# Revit family: APB_SUPPLY
name_source: partatom
category: Mechanical Equipment
units: mm (PartAtom-declared; Revit-internal decimal feet)

## family parameters
Always vertical = Yes
Cut with Voids When Loaded = No
Part Type = Normal
Room Calculation Point = No
Round Connector Dimension = Use Diameter
Shared = No
Work Plane-Based = No

## types (5) — shared parameters
0 = 0' - 0"
1" = 0' - 1"
1.5 = 0' - 1 1/2"
135 = 135.00°
2" = 0' - 2"
2' = 2' - 0"
3" = 0' - 3"
4" = 0' - 4"
9" = 0' - 9"
90 = 90.00°
HALF = 0' - 0 1/2"
Manufacturer = Loren Cook Company
Model = APB-Supply
ONE EIGTH = 0' - 0 1/8"
Type Comments = Axia-Pac Wall Supply Ventilator Cast Aluminum Propeller Belt Drive
URL = www.lorencook.com

## per-type parameters (varying)
- 24_APB_SUPPLY: (A/2)-1"=1' - 2 27/32"; (A/2)-C-.5"=0' - 7 27/32"; (D_SUP/2)-(C/2)-.125"=0' - 11 1/2"; (SIZE/2)-.25"=0' - 11 3/4"; -((A/2)-C-.5")=-0' - 7 27/32"; -((SIZE/2)-.25")=-0' - 11 3/4"; -B=-1' - 7 1/16"; -B+1"=-1' - 5 1/16"; -C/2=-0' - 3 3/8"; -D=-0' - 2"; -D_PAC/2=-1' - 9 3/16"; -WH_B/2=-1' - 5"; A=2' - 6 3/16"; A/2=1' - 3 3/32"; A/3.5=0' - 8 5/8"; A/7=0' - 4 5/16"; A_PAC=2' - 9 1/2"; A_PAC/2=1' - 4 3/4"; B=1' - 7 1/16"; B/2=0' - 9 17/32"; B/4=0' - 4 25/32"; B_PAC=2' - 7"; B_PAC/2=1' - 3 1/2"; C=0' - 6 3/4"; C/2=0' - 3 3/8"; C_PAC=2' - 3 1/2"; C_PAC/2=1' - 1 3/4"; D=0' - 2"; D/2=0' - 1"; D_PAC=2' - 10 3/8"; D_PAC/2=1' - 1 3/16"; D_SUP=2' - 6"; D_SUP/2=1' - 3"; MOTOR=0' - 3"; SIZE=2' - 0"; SIZE/2=1' - 0"; WH_A=2' - 3 1/8"; WH_B=2' - 10"; WH_B/2=1' - 5"; WH_C=3' - 1"; WO_PAC=2' - 7 1/4"; WO_PAC/2=1' - 3 5/8"
- 30_APB_SUPPLY: (A/2)-1"=1' - 5 27/32"; (A/2)-C-.5"=0' - 10 27/32"; (D_SUP/2)-(C/2)-.125"=1' - 2 1/2"; (SIZE/2)-.25"=1' - 2 3/4"; -((A/2)-C-.5")=-0' - 10 27/32"; -((SIZE/2)-.25")=-1' - 2 3/4"; -B=-1' - 7 1/16"; -B+1"=-1' - 5 1/16"; -C/2=-0' - 3 3/8"; -D=-0' - 3"; -D_PAC/2=-1' - 11"; -WH_B/2=-1' - 8"; A=3' - 0 3/16"; A/2=1' - 6 3/32"; A/3.5=0' - 10 11/32"; A/7=0' - 5 5/32"; A_PAC=3' - 3 1/2"; A_PAC/2=1' - 7 3/4"; B=1' - 7 1/16"; B/2=0' - 9 17/32"; B/4=0' - 4 25/32"; B_PAC=3' - 1"; B_PAC/2=1' - 6 1/2"; C=0' - 6 3/4"; C/2=0' - 3 3/8"; C_PAC=2' - 9 1/2"; C_PAC/2=1' - 4 3/4"; D=0' - 3"; D/2=0' - 1 1/2"; D_PAC=3' - 2"; D_PAC/2=1' - 3"; D_SUP=3' - 0"; D_SUP/2=1' - 6"; MOTOR=0' - 3 19/32"; SIZE=2' - 6"; SIZE/2=1' - 3"; WH_A=2' - 7 7/16"; WH_B=3' - 4"; WH_B/2=1' - 8"; WH_C=3' - 7"; WO_PAC=3' - 1 1/4"; WO_PAC/2=1' - 6 5/8"
- 36_APB_SUPPLY: (A/2)-1"=1' - 8 27/32"; (A/2)-C-.5"=1' - 1 7/32"; (D_SUP/2)-(C/2)-.125"=1' - 5 3/16"; (SIZE/2)-.25"=1' - 5 3/4"; -((A/2)-C-.5")=-1' - 1 7/32"; -((SIZE/2)-.25")=-1' - 5 3/4"; -B=-1' - 7 1/16"; -B+1"=-1' - 5 1/16"; -C/2=-0' - 3 11/16"; -D=-0' - 3"; -D_PAC/2=-1' - 11 3/4"; -WH_B/2=-1' - 11"; A=3' - 6 3/16"; A/2=1' - 9 3/32"; A/3.5=1' - 0 1/16"; A/7=0' - 6 1/32"; A_PAC=3' - 9 1/2"; A_PAC/2=1' - 10 3/4"; B=1' - 7 1/16"; B/2=0' - 9 17/32"; B/4=0' - 4 25/32"; B_PAC=3' - 7"; B_PAC/2=1' - 9 1/2"; C=0' - 7 3/8"; C/2=0' - 3 11/16"; C_PAC=3' - 3 1/2"; C_PAC/2=1' - 7 3/4"; D=0' - 3"; D/2=0' - 1 1/2"; D_PAC=3' - 3 1/2"; D_PAC/2=1' - 3 3/4"; D_SUP=3' - 6"; D_SUP/2=1' - 9"; MOTOR=0' - 4 3/16"; SIZE=3' - 0"; SIZE/2=1' - 6"; WH_A=2' - 11 11/16"; WH_B=3' - 10"; WH_B/2=1' - 11"; WH_C=4' - 1"; WO_PAC=3' - 7 1/4"; WO_PAC/2=1' - 9 5/8"
- 42_APB_SUPPLY: (A/2)-1"=1' - 11 27/32"; (A/2)-C-.5"=1' - 3 31/32"; (D_SUP/2)-(C/2)-.125"=1' - 8 1/16"; (SIZE/2)-.25"=1' - 8 3/4"; -((A/2)-C-.5")=-1' - 3 31/32"; -((SIZE/2)-.25")=-1' - 8 3/4"; -B=-1' - 8 11/16"; -B+1"=-1' - 6 11/16"; -C/2=-0' - 3 13/16"; -D=-0' - 3"; -D_PAC/2=-2' - 0 7/16"; -WH_B/2=-2' - 2"; A=4' - 0 3/16"; A/2=2' - 0 3/32"; A/3.5=1' - 1 25/32"; A/7=0' - 6 7/8"; A_PAC=4' - 3 1/2"; A_PAC/2=2' - 1 3/4"; B=1' - 8 11/16"; B/2=0' - 10 11/32"; B/4=0' - 5 3/16"; B_PAC=4' - 1 1/16"; B_PAC/2=2' - 0 17/32"; C=0' - 7 5/8"; C/2=0' - 3 13/16"; C_PAC=3' - 9 1/2"; C_PAC/2=1' - 10 3/4"; D=0' - 3"; D/2=0' - 1 1/2"; D_PAC=3' - 4 7/8"; D_PAC/2=1' - 4 7/16"; D_SUP=4' - 0"; D_SUP/2=2' - 0"; MOTOR=0' - 4 13/16"; SIZE=3' - 6"; SIZE/2=1' - 9"; WH_A=3' - 3 15/16"; WH_B=4' - 4"; WH_B/2=2' - 2"; WH_C=4' - 7"; WO_PAC=4' - 1 5/16"; WO_PAC/2=2' - 0 21/32"
- 48_APB_SUPPLY: (A/2)-1"=2' - 2 27/32"; (A/2)-C-.5"=1' - 6 31/32"; (D_SUP/2)-(C/2)-.125"=1' - 11 1/16"; (SIZE/2)-.25"=1' - 11 3/4"; -((A/2)-C-.5")=-1' - 6 31/32"; -((SIZE/2)-.25")=-1' - 11 3/4"; -B=-2' - 2 5/16"; -B+1"=-2' - 0 5/16"; -C/2=-0' - 3 13/16"; -D=-0' - 3"; -D_PAC/2=-2' - 5 7/16"; -WH_B/2=-2' - 5"; A=4' - 6 3/16"; A/2=2' - 3 3/32"; A/3.5=1' - 3 15/32"; A/7=0' - 7 3/4"; A_PAC=4' - 9 1/2"; A_PAC/2=2' - 4 3/4"; B=2' - 2 5/16"; B/2=1' - 1 5/32"; B/4=0' - 6 19/32"; B_PAC=4' - 7 1/16"; B_PAC/2=2' - 3 17/32"; C=0' - 7 5/8"; C/2=0' - 3 13/16"; C_PAC=4' - 3 1/2"; C_PAC/2=2' - 1 3/4"; D=0' - 3"; D/2=0' - 1 1/2"; D_PAC=4' - 2 7/8"; D_PAC/2=1' - 9 7/16"; D_SUP=4' - 6"; D_SUP/2=2' - 3"; MOTOR=0' - 5 13/32"; SIZE=4' - 0"; SIZE/2=2' - 0"; WH_A=3' - 8 3/16"; WH_B=4' - 10"; WH_B/2=2' - 5"; WH_C=5' - 1"; WO_PAC=4' - 7 5/16"; WO_PAC/2=2' - 3 21/32"

## geometry (parser evidence)
native form markers: Sweep x2
no freeform markers — native parametric forms only
